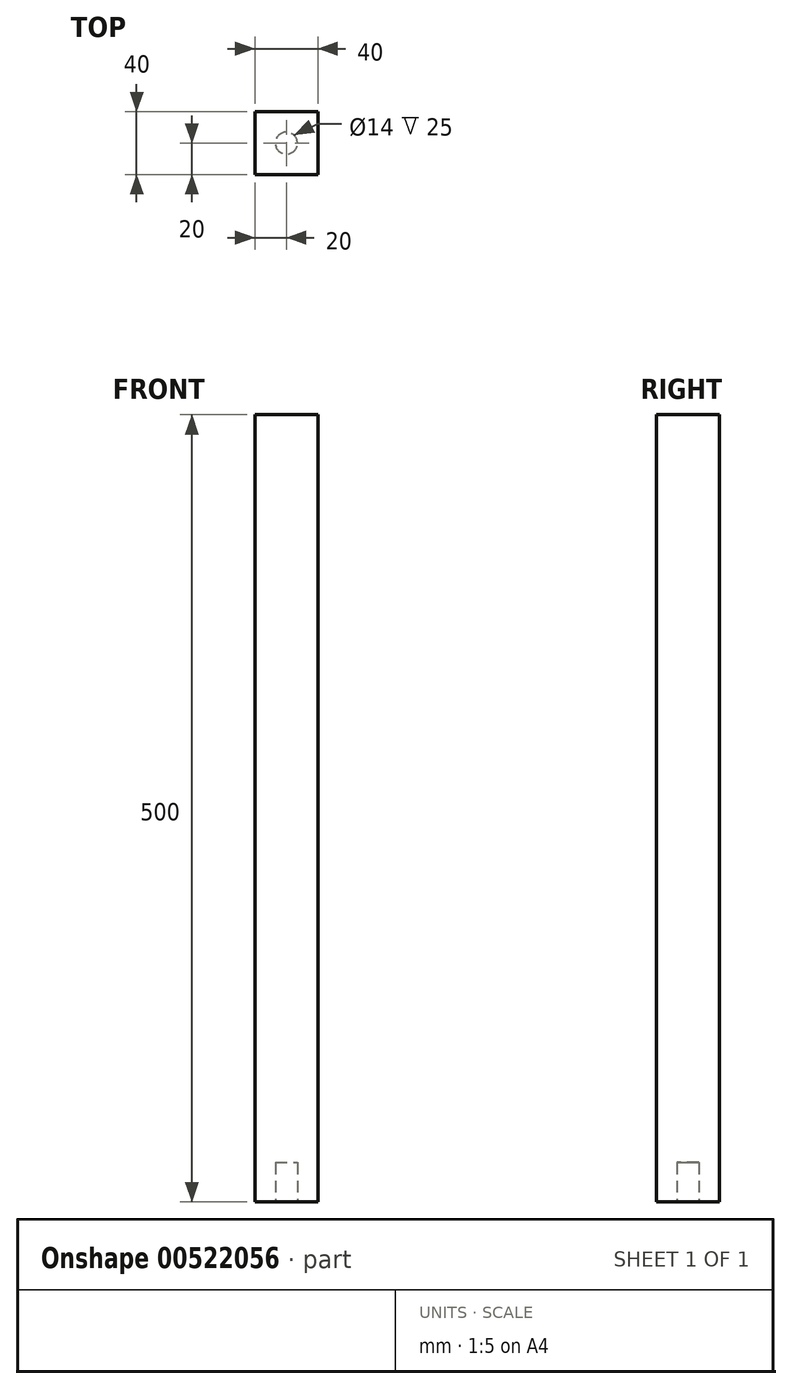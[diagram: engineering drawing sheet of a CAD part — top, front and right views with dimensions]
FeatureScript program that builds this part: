
annotation { "Feature Type Name" : "Feature", "Feature Type Description" : "" }
export const myFeature = defineFeature(function(context is Context, id is Id, definition is map)
    precondition{}
    {
        {
            var Q0;
            Q0=qCreatedBy(makeId("Top.planeOp"),FACE);
            var sketch = newSketch(context, id + "F0", { "sketchPlane" : qUnion([Q0])});
            skLineSegment(sketch, "E0.bottom", {"start": v(0, 0) * mm, "end": v(-40, 0) * mm});
            skLineSegment(sketch, "E0.top", {"start": v(0, -40) * mm, "end": v(-40, -40) * mm});
            skLineSegment(sketch, "E0.left", {"start": v(0, 0) * mm, "end": v(0, -40) * mm});
            skLineSegment(sketch, "E0.right", {"start": v(-40, 0) * mm, "end": v(-40, -40) * mm});
            skSolve(sketch);
        }
        {
            var Q0;
            Q0=makeQuery(id+"F0.imprint","IMPRINT",FACE,{"disambiguationData":[TD([[makeQuery(id+"F0.imprint","IMPRINT",EDGE,{"derivedFrom":sQuery(id+"F0.wireOp",EDGE,"E0.bottom")}),1.0]])]});
            extrude(context, id + "F1", {"entities" : qUnion([Q0]), "depth" : 500 * mm, "offsetDistance" : 25 * mm});
        }
        {
            var Q0;
            Q0=makeQuery(id+"F1.opExtrude","CAP_FACE",FACE,{"disambiguationData":[OSD([sQuery(id+"F0.wireOp",EDGE,"E0.bottom"),sQuery(id+"F0.wireOp",EDGE,"E0.top"),sQuery(id+"F0.wireOp",EDGE,"E0.left"),sQuery(id+"F0.wireOp",EDGE,"E0.right")])],"isStart":true});
            var sketch = newSketch(context, id + "F2", { "sketchPlane" : qUnion([Q0])});
            skCircle(sketch, "E1", {"center": v(-20, 20) * mm, "radius": 7 * mm});
            skLineSegment(sketch, "E2", {"start": v(-20, 40) * mm, "end": v(-20, 0) * mm, "construction": true});
            skSolve(sketch);
        }
        {
            var Q0;
            Q0=makeQuery(id+"F2.imprint","IMPRINT",FACE,{"disambiguationData":[TD([[makeQuery(id+"F2.imprint","IMPRINT",EDGE,{"derivedFrom":sQuery(id+"F2.wireOp",EDGE,"E1")}),1.0]])]});
            extrude(context, id + "F3", {"entities" : qUnion([Q0]), "operationType" : NewBodyOperationType.REMOVE, "oppositeDirection" : true, "depth" : 25 * mm, "offsetDistance" : 25 * mm});
        }
    });
